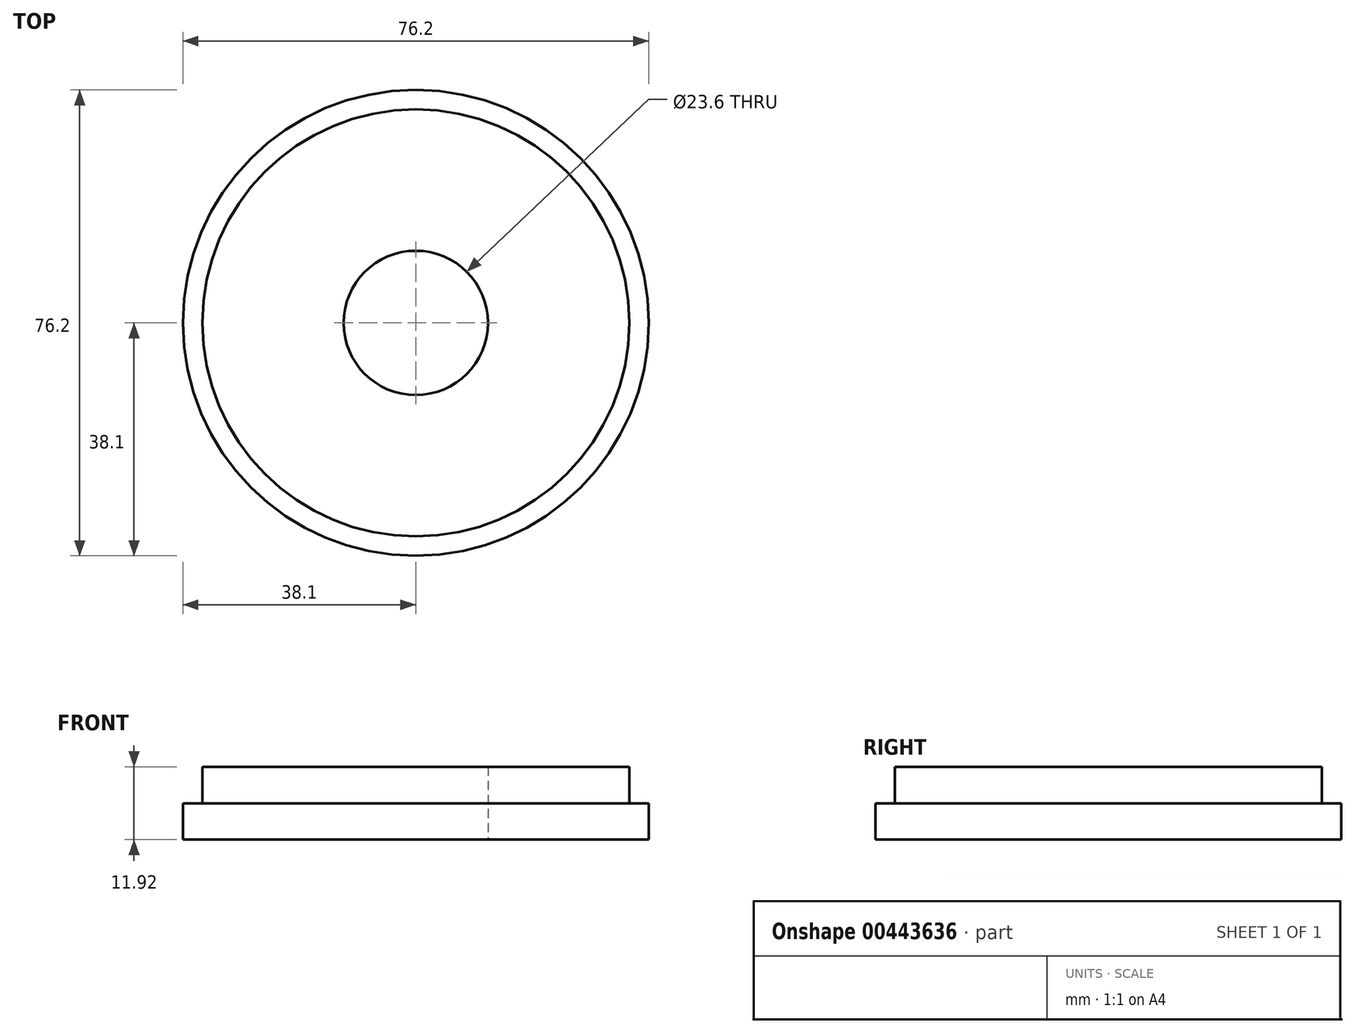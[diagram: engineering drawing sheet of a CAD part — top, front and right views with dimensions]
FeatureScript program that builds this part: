
annotation { "Feature Type Name" : "Feature", "Feature Type Description" : "" }
export const myFeature = defineFeature(function(context is Context, id is Id, definition is map)
    precondition{}
    {
        {
            var Q0;
            Q0=qCreatedBy(makeId("Top.planeOp"),FACE);
            var sketch = newSketch(context, id + "F0", { "sketchPlane" : qUnion([Q0])});
            skCircle(sketch, "E0", {"center": v(0, 0) * mm, "radius": 38.1 * mm});
            skCircle(sketch, "E1", {"center": v(0, 0) * mm, "radius": 11.8 * mm});
            skSolve(sketch);
        }
        {
            var Q0;
            Q0 = qSketchRegion(id + "F0", true);
            extrude(context, id + "F1", {"entities" : qUnion([Q0]), "depth" : 5.96 * mm});
        }
        {
            var Q0;
            Q0=makeQuery(id+"F1.opExtrude","CAP_FACE",FACE,{"disambiguationData":[OSD([sQuery(id+"F0.wireOp",EDGE,"E0")])],"isStart":false});
            var sketch = newSketch(context, id + "F2", { "sketchPlane" : qUnion([Q0])});
            skCircle(sketch, "E2", {"center": v(0, 0) * mm, "radius": 34.92 * mm});
            skCircle(sketch, "E3", {"center": v(0, 0) * mm, "radius": 11.8 * mm});
            skSolve(sketch);
        }
        {
            var Q0;
            Q0 = qSketchRegion(id + "F2", true);
            extrude(context, id + "F3", {"entities" : qUnion([Q0]), "operationType" : NewBodyOperationType.ADD, "depth" : 5.96 * mm});
        }
    });
